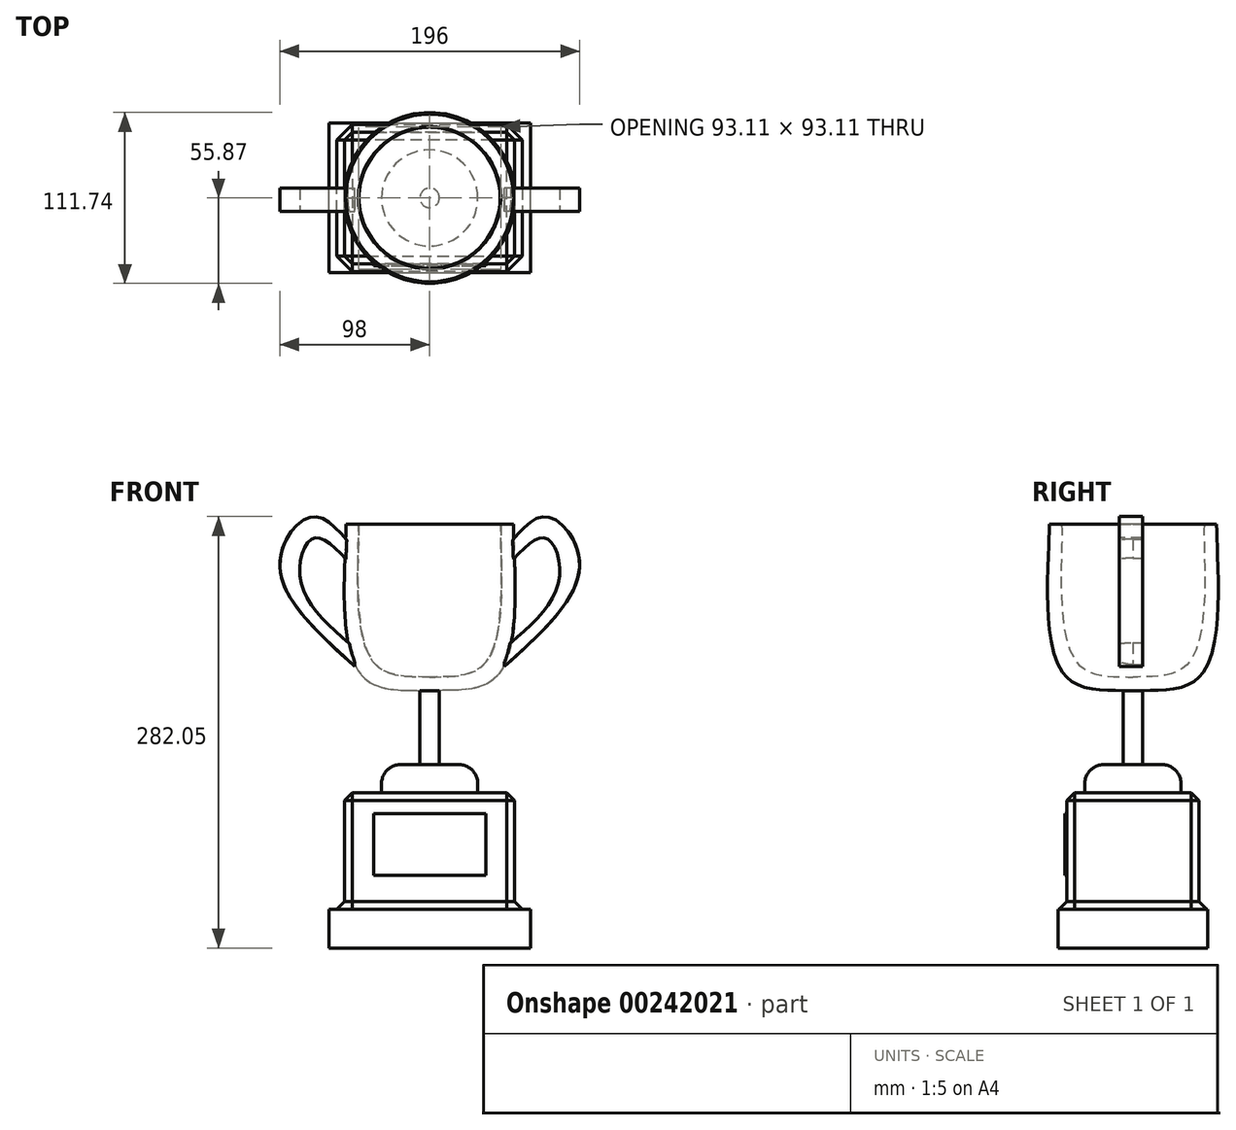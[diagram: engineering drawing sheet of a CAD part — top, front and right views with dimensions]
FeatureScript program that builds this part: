
annotation { "Feature Type Name" : "Feature", "Feature Type Description" : "" }
export const myFeature = defineFeature(function(context is Context, id is Id, definition is map)
    precondition{}
    {
        {
            var Q0;
            Q0=qCreatedBy(makeId("Front.planeOp"),FACE);
            var sketch = newSketch(context, id + "F0", { "sketchPlane" : qUnion([Q0])});
            skFitSpline(sketch, "E0", {"points": [v(0, 26.86) * mm, v(-37.65, 37.92) * mm, v(-46.56, 127.1) * mm], "startDerivative": vector(-80.74, 8.78) * mm, "endDerivative": vector(-5.05, 73.8) * mm});
            skLineSegment(sketch, "E1", {"start": v(-46.56, 127.1) * mm, "end": v(-54.72, 127.1) * mm});
            skFitSpline(sketch, "E2", {"points": [v(-54.72, 127.1) * mm, v(-45.99, 30.06) * mm, v(0, 18) * mm], "startDerivative": vector(1.88, -92.9) * mm, "endDerivative": vector(105.66, -8.08) * mm});
            skLineSegment(sketch, "E3", {"start": v(0, 26.86) * mm, "end": v(0, 18) * mm});
            skLineSegment(sketch, "E4", {"start": v(-6.38, 18.25) * mm, "end": v(-6.38, -30.07) * mm});
            skLineSegment(sketch, "E5", {"start": v(-6.38, -30.07) * mm, "end": v(0, -30.07) * mm});
            skLineSegment(sketch, "E6", {"start": v(0, -30.07) * mm, "end": v(0, 18) * mm});
            skLineSegment(sketch, "E7", {"start": v(-6.38, -30.07) * mm, "end": v(-31.48, -30.07) * mm});
            skLineSegment(sketch, "E8", {"start": v(-31.48, -30.07) * mm, "end": v(-31.48, -48.53) * mm});
            skLineSegment(sketch, "E9", {"start": v(-31.48, -48.53) * mm, "end": v(0, -48.53) * mm});
            skLineSegment(sketch, "E10", {"start": v(0, -48.53) * mm, "end": v(0, -30.07) * mm});
            skSolve(sketch);
        }
        {
            var Q0;
            Q0=qCreatedBy(makeId("Front.planeOp"),FACE);
            var sketch = newSketch(context, id + "F1", { "sketchPlane" : qUnion([Q0])});
            skLineSegment(sketch, "E11", {"start": v(0, 75.86) * mm, "end": v(0, -59.28) * mm});
            skSolve(sketch);
        }
        {
            var Q0;
            {var subQ2=sQuery(id+"F0.wireOp",EDGE,"E4");Q0=makeQuery(id+"F0.imprint","IMPRINT",FACE,{"disambiguationData":[TD([[makeQuery(id+"F0.imprint","IMPRINT",EDGE,{"derivedFrom":subQ2}),1.0]])]});}
            var Q1;
            Q1=makeQuery(id+"F0.imprint","IMPRINT",FACE,{"disambiguationData":[TD([[makeQuery(id+"F0.imprint","IMPRINT",EDGE,{"derivedFrom":sQuery(id+"F0.wireOp",EDGE,"E0")}),1.0]])]});
            var Q2;
            Q2=makeQuery(id+"F0.imprint","IMPRINT",FACE,{"disambiguationData":[TD([[makeQuery(id+"F0.imprint","IMPRINT",EDGE,{"derivedFrom":sQuery(id+"F0.wireOp",EDGE,"E5")}),-1.0]])]});
            var Q3;
            Q3=sQuery(id+"F1.wireOp",EDGE,"E11");
            revolve(context, id + "F2", {"entities" : qUnion([Q0, Q1, Q2]), "axis" : qUnion([Q3]), "revolveType" : RevolveType.FULL});
        }
        {
            var Q0;
            Q0=makeQuery(id+"F2.opRevolve","SWEPT_EDGE",EDGE,{"disambiguationData":[OSD([sQuery(id+"F0.wireOp",EDGE,"E7"),sQuery(id+"F0.wireOp",EDGE,"E8")])]});
            fillet(context, id + "F3", {"entities" : qUnion([Q0]), "radius" : 12.7 * mm, "tangentPropagation" : true, "allowEdgeOverflow" : false});
        }
        {
            var Q0;
            Q0=makeQuery(id+"F2.opRevolve","SWEPT_FACE",FACE,{"disambiguationData":[OSD([sQuery(id+"F0.wireOp",EDGE,"E9")])]});
            var sketch = newSketch(context, id + "F4", { "sketchPlane" : qUnion([Q0])});
            skLineSegment(sketch, "E12.bottom", {"start": v(-55.53, 43.07) * mm, "end": v(55.53, 43.07) * mm});
            skLineSegment(sketch, "E12.top", {"start": v(-55.53, -43.07) * mm, "end": v(55.53, -43.07) * mm});
            skLineSegment(sketch, "E12.left", {"start": v(-55.53, 43.07) * mm, "end": v(-55.53, -43.07) * mm});
            skLineSegment(sketch, "E12.right", {"start": v(55.53, 43.07) * mm, "end": v(55.53, -43.07) * mm});
            skPoint(sketch, "E12.middle", {"position": v(0, 0) * mm});
            skSolve(sketch);
        }
        {
            var Q0;
            Q0=makeQuery(id+"F4.imprint","IMPRINT",FACE,{"disambiguationData":[TD([[makeQuery(id+"F4.imprint","IMPRINT",EDGE,{"derivedFrom":sQuery(id+"F4.wireOp",EDGE,"E12.bottom")}),-1.0]])]});
            var Q1;
            Q1=makeQuery(id+"F4.imprint","IMPRINT",FACE,{"disambiguationData":[TD([[makeQuery(id+"F4.imprint","IMPRINT",EDGE,{"derivedFrom":makeQuery(id+"F2.opRevolve","SWEPT_EDGE",EDGE,{"disambiguationData":[OSD([sQuery(id+"F0.wireOp",EDGE,"E8"),sQuery(id+"F0.wireOp",EDGE,"E9")])]})}),-1.0]])]});
            extrude(context, id + "F5", {"entities" : qUnion([Q0, Q1]), "depth" : 76.2 * mm});
        }
        {
            var Q0;
            Q0=makeQuery(id+"F5.opExtrude","CAP_FACE",FACE,{"disambiguationData":[OSD([sQuery(id+"F4.wireOp",EDGE,"E12.bottom"),sQuery(id+"F4.wireOp",EDGE,"E12.top"),sQuery(id+"F4.wireOp",EDGE,"E12.left"),sQuery(id+"F4.wireOp",EDGE,"E12.right")])],"isStart":false});
            var sketch = newSketch(context, id + "F6", { "sketchPlane" : qUnion([Q0])});
            skLineSegment(sketch, "E13.bottom", {"start": v(-65.97, 48.91) * mm, "end": v(65.97, 48.91) * mm});
            skLineSegment(sketch, "E13.top", {"start": v(-65.97, -48.91) * mm, "end": v(65.97, -48.91) * mm});
            skLineSegment(sketch, "E13.left", {"start": v(-65.97, 48.91) * mm, "end": v(-65.97, -48.91) * mm});
            skLineSegment(sketch, "E13.right", {"start": v(65.97, 48.91) * mm, "end": v(65.97, -48.91) * mm});
            skPoint(sketch, "E13.middle", {"position": v(0, 0) * mm});
            skSolve(sketch);
        }
        {
            var Q0;
            Q0=makeQuery(id+"F6.imprint","IMPRINT",FACE,{"disambiguationData":[TD([[makeQuery(id+"F6.imprint","IMPRINT",EDGE,{"derivedFrom":sQuery(id+"F6.wireOp",EDGE,"E13.bottom")}),-1.0]])]});
            var Q1;
            Q1=makeQuery(id+"F6.imprint","IMPRINT",FACE,{"disambiguationData":[TD([[makeQuery(id+"F6.imprint","IMPRINT",EDGE,{"derivedFrom":makeQuery(id+"F5.opExtrude","CAP_EDGE",EDGE,{"disambiguationData":[OSD([sQuery(id+"F4.wireOp",EDGE,"E12.bottom")])],"isStart":false})}),-1.0]])]});
            extrude(context, id + "F7", {"entities" : qUnion([Q0, Q1]), "operationType" : NewBodyOperationType.ADD, "depth" : 25.4 * mm});
        }
        {
            var Q0;
            Q0=makeQuery(id+"F5.opExtrude","SWEPT_FACE",FACE,{"disambiguationData":[OSD([sQuery(id+"F4.wireOp",EDGE,"E12.bottom")])]});
            var sketch = newSketch(context, id + "F8", { "sketchPlane" : qUnion([Q0])});
            skLineSegment(sketch, "E14.bottom", {"start": v(-36.63, -62.38) * mm, "end": v(36.63, -62.38) * mm});
            skLineSegment(sketch, "E14.top", {"start": v(-36.63, -102.68) * mm, "end": v(36.63, -102.68) * mm});
            skLineSegment(sketch, "E14.left", {"start": v(-36.63, -62.38) * mm, "end": v(-36.63, -102.68) * mm});
            skLineSegment(sketch, "E14.right", {"start": v(36.63, -62.38) * mm, "end": v(36.63, -102.68) * mm});
            skPoint(sketch, "E14.middle", {"position": v(0, -82.53) * mm});
            skSolve(sketch);
        }
        {
            var Q0;
            Q0=makeQuery(id+"F8.imprint","IMPRINT",FACE,{"disambiguationData":[TD([[makeQuery(id+"F8.imprint","IMPRINT",EDGE,{"derivedFrom":sQuery(id+"F8.wireOp",EDGE,"E14.bottom")}),-1.0]])]});
            extrude(context, id + "F9", {"entities" : qUnion([Q0]), "depth" : 1.27 * mm});
        }
        {
            var Q0;
            Q0=qCreatedBy(makeId("Front.planeOp"),FACE);
            var sketch = newSketch(context, id + "F10", { "sketchPlane" : qUnion([Q0])});
            skFitSpline(sketch, "E15", {"points": [v(52.1, 113.93) * mm, v(76.98, 131.8) * mm, v(98, 100.27) * mm, v(48.95, 34.06) * mm], "startDerivative": vector(89.7, 108.12) * mm, "endDerivative": vector(-167.97, -151.3) * mm});
            skFitSpline(sketch, "E16", {"points": [v(52.1, 101.32) * mm, v(75.93, 117.78) * mm, v(84.33, 89.76) * mm, v(48.95, 45.97) * mm], "startDerivative": vector(88.49, 94.98) * mm, "endDerivative": vector(-117.4, -98.85) * mm});
            skLineSegment(sketch, "E17", {"start": v(52.1, 113.93) * mm, "end": v(52.1, 98.06) * mm});
            skLineSegment(sketch, "E18", {"start": v(52.1, 98.06) * mm, "end": v(52.1, 101.32) * mm});
            skLineSegment(sketch, "E19", {"start": v(48.95, 45.97) * mm, "end": v(48.95, 34.06) * mm});
            skSolve(sketch);
        }
        {
            var Q0;
            Q0=makeQuery(id+"F10.imprint","IMPRINT",FACE,{"disambiguationData":[TD([[makeQuery(id+"F10.imprint","IMPRINT",EDGE,{"derivedFrom":sQuery(id+"F10.wireOp",EDGE,"E15")}),-1.0]])]});
            extrude(context, id + "F11", {"entities" : qUnion([Q0]), "operationType" : NewBodyOperationType.ADD, "depth" : 8.9 * mm});
        }
        {
            var Q0;
            Q0=makeQuery(id+"F11.opExtrude","CAP_FACE",FACE,{"disambiguationData":[OSD([sQuery(id+"F10.wireOp",EDGE,"E15"),sQuery(id+"F10.wireOp",EDGE,"E16"),sQuery(id+"F10.wireOp",EDGE,"E17"),sQuery(id+"F10.wireOp",EDGE,"E19")])],"isStart":true});
            extrude(context, id + "F12", {"entities" : qUnion([Q0]), "operationType" : NewBodyOperationType.ADD, "oppositeDirection" : true, "depth" : 6.35 * mm, "hasSecondDirection" : true, "secondDirectionOppositeDirection" : false, "secondDirectionDepth" : 6.35 * mm});
        }
        {
            var Q0;
            Q0=makeQuery(id+"F2.opRevolve","SWEPT_BODY",BODY,{"disambiguationData":[OSD([sQuery(id+"F0.wireOp",EDGE,"E0"),sQuery(id+"F0.wireOp",EDGE,"E1"),sQuery(id+"F0.wireOp",EDGE,"E2"),sQuery(id+"F0.wireOp",EDGE,"E3"),sQuery(id+"F0.wireOp",EDGE,"E4"),sQuery(id+"F0.wireOp",EDGE,"E6"),sQuery(id+"F0.wireOp",EDGE,"E7"),sQuery(id+"F0.wireOp",EDGE,"E8"),sQuery(id+"F0.wireOp",EDGE,"E9"),sQuery(id+"F0.wireOp",EDGE,"E10")])]});
            var Q1;
            Q1=qCreatedBy(makeId("Right.planeOp"),FACE);
            mirror(context, id + "F13", {"entities" : qUnion([Q0]), "mirrorPlane" : qUnion([Q1])});
        }
        {
            var Q0;
            Q0=makeQuery(id+"F5.opExtrude","SWEPT_FACE",FACE,{"disambiguationData":[OSD([sQuery(id+"F4.wireOp",EDGE,"E12.left")])]});
            var Q1;
            Q1=makeQuery(id+"F5.opExtrude","SWEPT_FACE",FACE,{"disambiguationData":[OSD([sQuery(id+"F4.wireOp",EDGE,"E12.right")])]});
            var Q2;
            Q2=makeQuery(id+"F5.opExtrude","SWEPT_FACE",FACE,{"disambiguationData":[OSD([sQuery(id+"F4.wireOp",EDGE,"E12.bottom")])]});
            var Q3;
            Q3=makeQuery(id+"F5.opExtrude","SWEPT_FACE",FACE,{"disambiguationData":[OSD([sQuery(id+"F4.wireOp",EDGE,"E12.top")])]});
            chamfer(context, id + "F14", {"entities" : qUnion([Q0, Q1, Q2, Q3]), "width" : 5.08 * mm, "tangentPropagation" : true});
        }
    });
